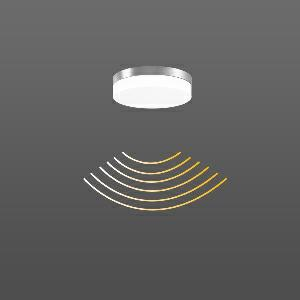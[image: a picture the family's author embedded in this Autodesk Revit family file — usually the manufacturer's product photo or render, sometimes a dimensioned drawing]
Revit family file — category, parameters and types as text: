
# Revit family: flat_slim_round_312135_004_1_19_904c
name_source: partatom
category: Lighting Fixtures
units: mm (PartAtom-declared; Revit-internal decimal feet)

## family parameters
Cut with Voids When Loaded = No
Host = Face
Light Source = No
Part Type = Normal
Room Calculation Point = No
Round Connector Dimension = Use Diameter
Shared = No

## types (1)
- FLAT SLIM round (1 x LED Modul 840, 1100 lm, 4000)
    Apparent Load = 12 VA
    CIE Flux Codes = 43 74 92 91 100
    Color Rendering = 80
    Color Temperature = 4000
    Default Elevation = 1800 mm
    Height = 63 mm
    Lamp = 1 x LED Modul 840
    Lamp Light Flux = 1100 lm
    Lamp count = 1
    Length = 230 mm
    Lifetime = 50000 h
    Luminous efficacy = 92 lm/W
    Manufacturer = RZB
    ModVariant = No
    Model = 312135.004.1.19
    Mounting Place = Ceiling, Wall
    Mounting Type = Surface mounted
    Number of Poles = 1
    OnlyDefault = Yes
    Power Factor = 1
    Product Name = FLAT SLIM round
    Product group = Surface mounted ceiling and wall luminaires
    ProductGroupID = 305
    Protection Class = Protection class I
    Protection Degree = IP 65
    RLX_Detail_Level = 1
    RLX_Emergency_Light_Flux = 0 lm
    RLX_Emergency_Type = 0
    RLX_Emergency_Type_DB = No
    RlxData = <blob elided: 32089 chars, md5=90801610>
    Socket = socket
    Standby Power = 0 W
    System Light Flux = 1100 lm
    System Power = 12 W
    Type Comments = Product without accessories
    Type Image = 312132.004.19.jpg
    URL = http://relux.com
    VarID = ---
    Voltage = 230 V
    Voltage Range = 220-240 V
    Weight = 0.00 kg
    Width = 0 mm  [stored 0 ft]

note: [stored X ft] marks values corroborated as IEEE doubles in the binary element streams (Revit-internal decimal feet)

## geometry (parser evidence)
native form markers: Blend x4, Sweep x12
no freeform markers — native parametric forms only
